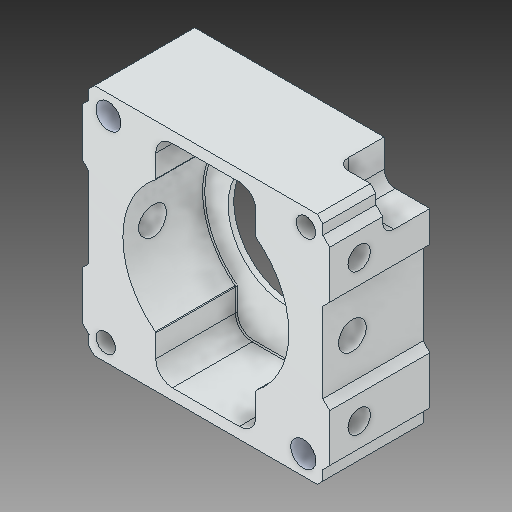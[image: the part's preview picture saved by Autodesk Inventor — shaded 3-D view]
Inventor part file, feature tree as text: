
AUTODESK INVENTOR PART (.ipt)
format: ipt  version: 2017 (Build 210142000, 142)  size: 273,408 bytes
history: native  units: in
note: dims shown in document units (in); Inventor stores cm internally (conversion verified against a paired STEP export)
features: chamfer x1
ambient origin geometry x8: Origin, YZ Plane, XZ Plane, XY Plane, X Axis, Y Axis, Z Axis, Center Point
bodies: Solid1 (feature_tree)
feature tree (1):
  chamfer  "Chamfer4"  [1 undecoded]
note: 1 required parameter value undecoded (feature->parameter linkage not recoverable at this tier; creation-order binding heuristic only, values carry confidence <= 0.55)
